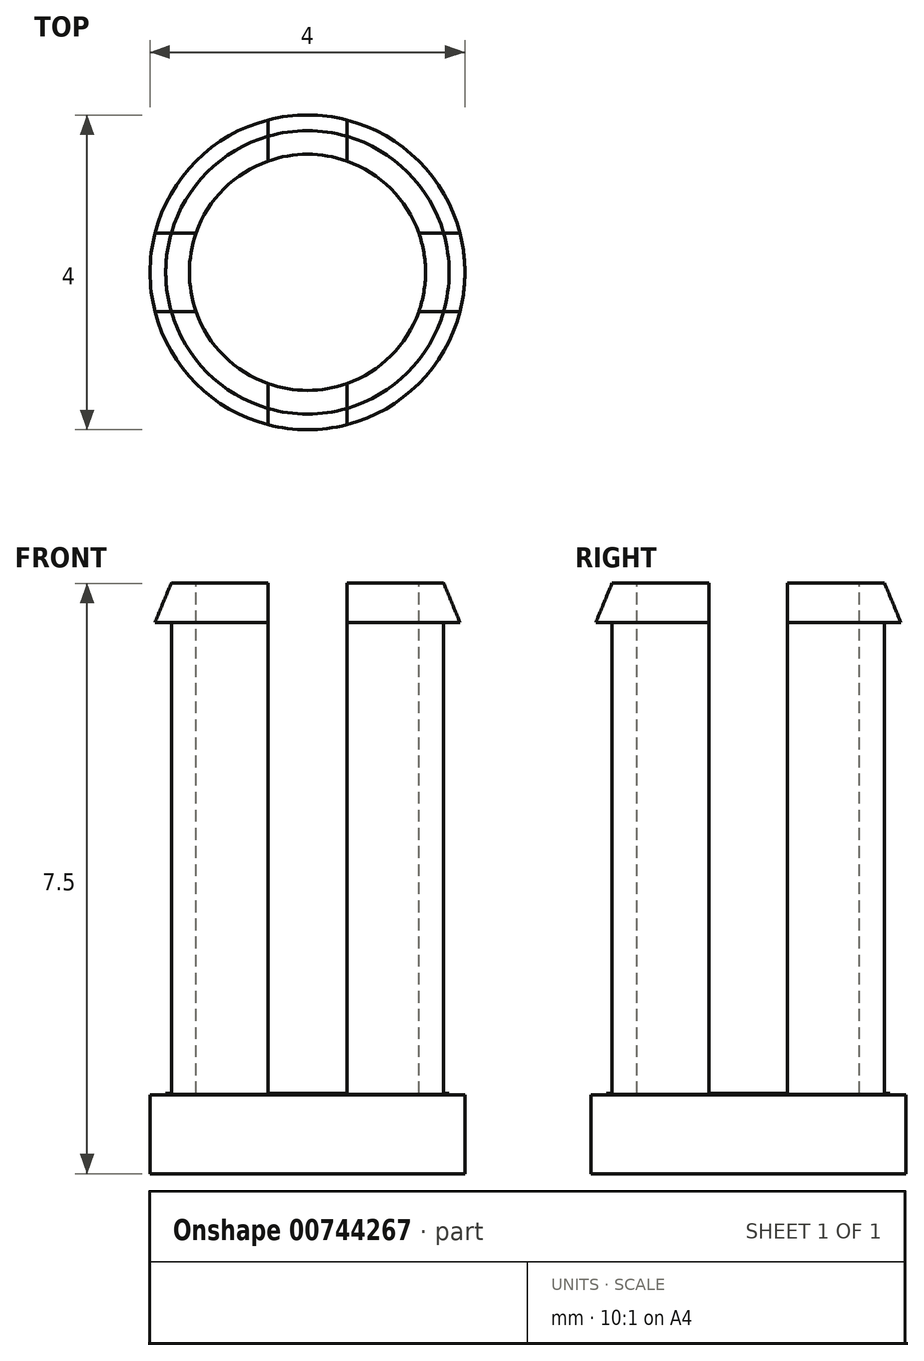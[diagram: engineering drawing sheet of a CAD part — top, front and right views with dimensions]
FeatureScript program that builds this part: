
annotation { "Feature Type Name" : "Feature", "Feature Type Description" : "" }
export const myFeature = defineFeature(function(context is Context, id is Id, definition is map)
    precondition{}
    {
        {
            var Q0;
            Q0=qCreatedBy(makeId("Top.planeOp"),FACE);
            var sketch = newSketch(context, id + "F0", { "sketchPlane" : qUnion([Q0])});
            skCircle(sketch, "E0", {"center": v(0, 0) * mm, "radius": 2 * mm});
            skSolve(sketch);
        }
        {
            var Q0;
            Q0=makeQuery(id+"F0.imprint","IMPRINT",FACE,{"disambiguationData":[TD([[makeQuery(id+"F0.imprint","IMPRINT",EDGE,{"derivedFrom":sQuery(id+"F0.wireOp",EDGE,"E0")}),1.0]])]});
            extrude(context, id + "F1", {"entities" : qUnion([Q0]), "depth" : 1 * mm, "offsetDistance" : 25 * mm});
        }
        {
            var Q0;
            Q0=qCreatedBy(makeId("Front.planeOp"),FACE);
            var sketch = newSketch(context, id + "F2", { "sketchPlane" : qUnion([Q0])});
            skLineSegment(sketch, "E1", {"start": v(0, 7.5) * mm, "end": v(1.8, 7.5) * mm});
            skLineSegment(sketch, "E2", {"start": v(1.8, 7.5) * mm, "end": v(2, 7) * mm});
            skLineSegment(sketch, "E3", {"start": v(2, 7) * mm, "end": v(1.8, 7) * mm});
            skLineSegment(sketch, "E4", {"start": v(1.8, 7) * mm, "end": v(1.8, 1) * mm});
            skLineSegment(sketch, "E5", {"start": v(1.8, 1) * mm, "end": v(0, 1) * mm});
            skLineSegment(sketch, "E6", {"start": v(0, 1) * mm, "end": v(0, 7.5) * mm});
            skSolve(sketch);
        }
        {
            var Q0;
            Q0=makeQuery(id+"F2.imprint","IMPRINT",FACE,{"disambiguationData":[TD([[makeQuery(id+"F2.imprint","IMPRINT",EDGE,{"derivedFrom":sQuery(id+"F2.wireOp",EDGE,"E1")}),-1.0]])]});
            var Q1;
            Q1=makeQuery(id+"F1.opExtrude","CAP_EDGE",EDGE,{"disambiguationData":[OSD([sQuery(id+"F0.wireOp",EDGE,"E0")])],"isStart":true});
            revolve(context, id + "F3", {"surfaceOperationType" : NewSurfaceOperationType.NEW, "entities" : qUnion([Q0]), "axis" : qUnion([Q1]), "revolveType" : RevolveType.FULL});
        }
        {
            var Q0;
            Q0=makeQuery(id+"F3.opRevolve","SWEPT_FACE",FACE,{"disambiguationData":[OSD([sQuery(id+"F2.wireOp",EDGE,"E1")])]});
            var sketch = newSketch(context, id + "F4", { "sketchPlane" : qUnion([Q0])});
            skCircle(sketch, "E7", {"center": v(0, 0) * mm, "radius": 1.5 * mm});
            skSolve(sketch);
        }
        {
            var Q0;
            Q0=makeQuery(id+"F4.imprint","IMPRINT",FACE,{"disambiguationData":[TD([[makeQuery(id+"F4.imprint","IMPRINT",EDGE,{"derivedFrom":sQuery(id+"F4.wireOp",EDGE,"E7")}),1.0]])]});
            extrude(context, id + "F5", {"entities" : qUnion([Q0]), "operationType" : NewBodyOperationType.REMOVE, "oppositeDirection" : true, "depth" : 6.5 * mm, "offsetDistance" : 25 * mm});
        }
        {
            var Q0;
            Q0=qCreatedBy(makeId("Top.planeOp"),FACE);
            cPlane(context, id + "F6", {"entities" : qUnion([Q0]), "cplaneType" : CPlaneType.OFFSET, "offset" : 7.52 * mm, "width" : 150 * mm, "height" : 150 * mm});
        }
        {
            var Q0;
            Q0=qCreatedBy(id+"F6.planeOp",FACE);
            var sketch = newSketch(context, id + "F7", { "sketchPlane" : qUnion([Q0])});
            skLineSegment(sketch, "E8.bottom", {"start": v(2.5, -0.5) * mm, "end": v(-2.5, -0.5) * mm});
            skLineSegment(sketch, "E8.top", {"start": v(2.5, 0.5) * mm, "end": v(-2.5, 0.5) * mm});
            skLineSegment(sketch, "E8.left", {"start": v(2.5, -0.5) * mm, "end": v(2.5, 0.5) * mm});
            skLineSegment(sketch, "E8.right", {"start": v(-2.5, -0.5) * mm, "end": v(-2.5, 0.5) * mm});
            skPoint(sketch, "E8.middle", {"position": v(0, 0) * mm});
            skLineSegment(sketch, "E9.bottom", {"start": v(0.5, -2.5) * mm, "end": v(-0.5, -2.5) * mm});
            skLineSegment(sketch, "E9.top", {"start": v(0.5, 2.5) * mm, "end": v(-0.5, 2.5) * mm});
            skLineSegment(sketch, "E9.left", {"start": v(0.5, -2.5) * mm, "end": v(0.5, 2.5) * mm});
            skLineSegment(sketch, "E9.right", {"start": v(-0.5, -2.5) * mm, "end": v(-0.5, 2.5) * mm});
            skSolve(sketch);
        }
        {
            var Q0;
            {var subQ0=sQuery(id+"F7.wireOp",EDGE,"E8.right");Q0=makeQuery(id+"F7.imprint","IMPRINT",FACE,{"disambiguationData":[TD([[makeQuery(id+"F7.imprint","IMPRINT",EDGE,{"derivedFrom":subQ0}),-1.0]])]});}
            var Q1;
            {var subQ5=sQuery(id+"F7.wireOp",EDGE,"E9.top");Q1=makeQuery(id+"F7.imprint","IMPRINT",FACE,{"disambiguationData":[TD([[makeQuery(id+"F7.imprint","IMPRINT",EDGE,{"derivedFrom":subQ5}),1.0]])]});}
            var Q2;
            {var subQ0=sQuery(id+"F7.wireOp",EDGE,"E8.left");Q2=makeQuery(id+"F7.imprint","IMPRINT",FACE,{"disambiguationData":[TD([[makeQuery(id+"F7.imprint","IMPRINT",EDGE,{"derivedFrom":subQ0}),1.0]])]});}
            var Q3;
            {var subQ5=sQuery(id+"F7.wireOp",EDGE,"E9.bottom");Q3=makeQuery(id+"F7.imprint","IMPRINT",FACE,{"disambiguationData":[TD([[makeQuery(id+"F7.imprint","IMPRINT",EDGE,{"derivedFrom":subQ5}),-1.0]])]});}
            extrude(context, id + "F8", {"entities" : qUnion([Q0, Q1, Q2, Q3]), "operationType" : NewBodyOperationType.REMOVE, "oppositeDirection" : true, "depth" : 6.5 * mm, "offsetDistance" : 25 * mm});
        }
    });
